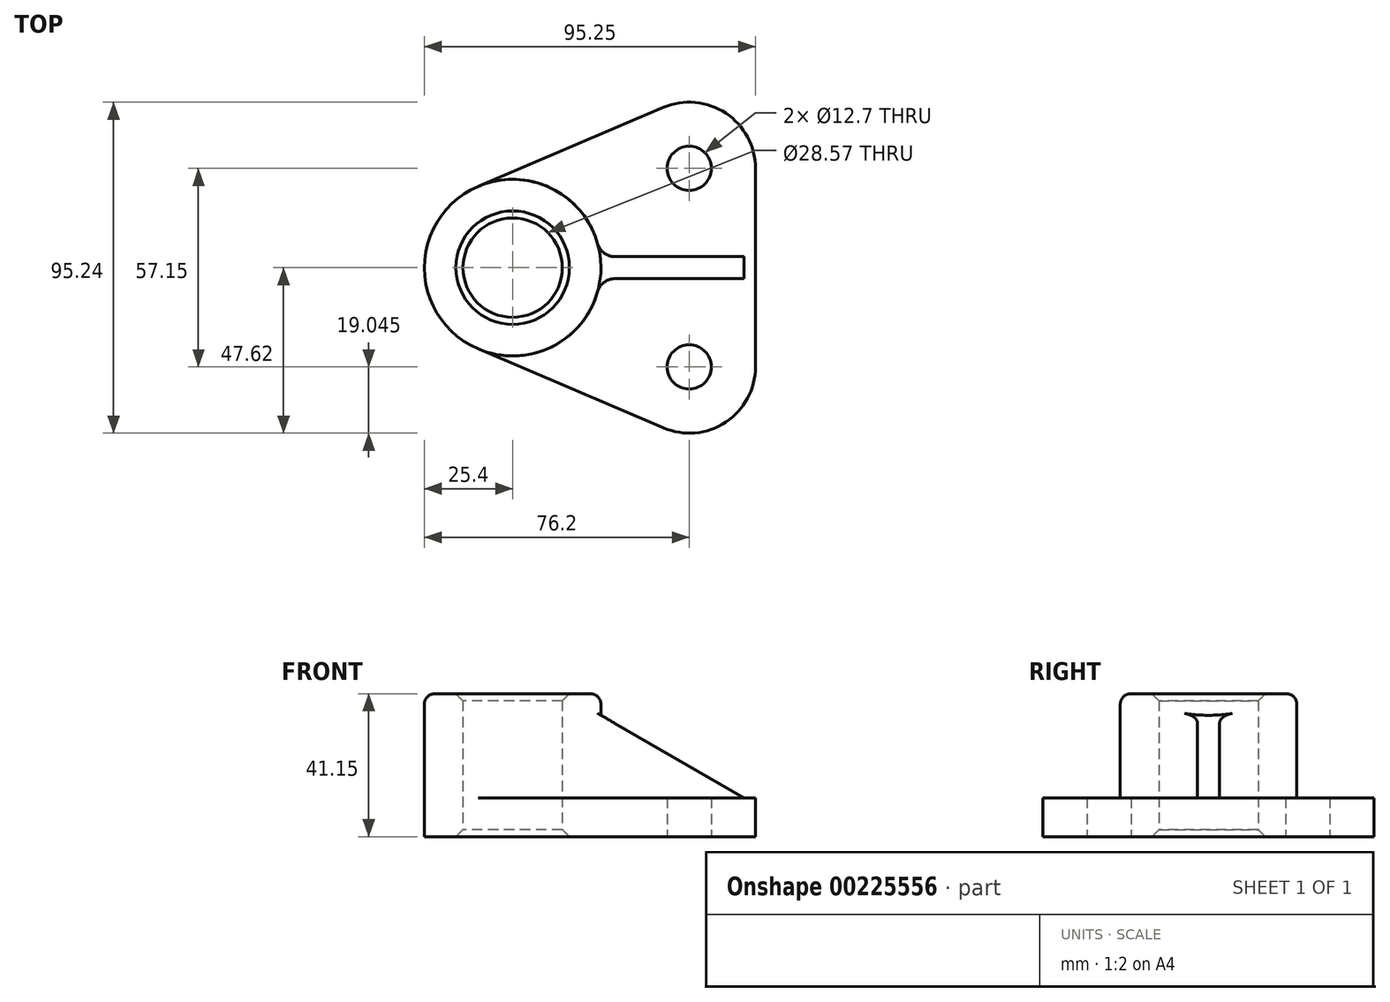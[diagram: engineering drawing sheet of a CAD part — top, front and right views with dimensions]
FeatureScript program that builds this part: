
annotation { "Feature Type Name" : "Feature", "Feature Type Description" : "" }
export const myFeature = defineFeature(function(context is Context, id is Id, definition is map)
    precondition{}
    {
        {
            var Q0;
            Q0=qCreatedBy(makeId("Top.planeOp"),FACE);
            var sketch = newSketch(context, id + "F0", { "sketchPlane" : qUnion([Q0])});
            skCircle(sketch, "E0", {"center": v(0, 0) * mm, "radius": 25.4 * mm});
            skCircle(sketch, "E1", {"center": v(0, 0) * mm, "radius": 14.29 * mm});
            skLineSegment(sketch, "E2", {"start": v(0, 0) * mm, "end": v(50.8, 0) * mm, "construction": true});
            skCircle(sketch, "E3", {"center": v(50.8, 28.58) * mm, "radius": 6.35 * mm});
            skArc(sketch, "E4", {"start": v(69.85, 28.58) * mm, "mid": v(61.3, 44.47) * mm, "end": v(43.33, 46.1) * mm});
            skLineSegment(sketch, "E5", {"start": v(-9.97, 23.36) * mm, "end": v(43.33, 46.1) * mm});
            skLineSegment(sketch, "E6", {"start": v(69.85, 28.58) * mm, "end": v(69.85, 0) * mm});
            skLineSegment(sketch, "E7", {"start": v(50.8, 0) * mm, "end": v(86.08, 0) * mm, "construction": true});
            skLineSegment(sketch, "E8.MirrorCS", {"start": v(-9.97, -23.36) * mm, "end": v(43.33, -46.1) * mm});
            skArc(sketch, "E9.MirrorCS", {"start": v(69.85, -28.58) * mm, "mid": v(61.3, -44.47) * mm, "end": v(43.33, -46.1) * mm});
            skLineSegment(sketch, "E10.MirrorCS", {"start": v(69.85, -28.58) * mm, "end": v(69.85, 0) * mm});
            skCircle(sketch, "E11.MirrorC", {"center": v(50.8, -28.58) * mm, "radius": 6.35 * mm});
            skSolve(sketch);
        }
        {
            var Q0;
            Q0 = qSketchRegion(id + "F0", true);
            extrude(context, id + "F1", {"entities" : qUnion([Q0]), "depth" : 11.18 * mm});
        }
        {
            var Q0;
            Q0=makeQuery(id+"F1.opExtrude","CAP_FACE",FACE,{"disambiguationData":[OSD([sQuery(id+"F0.wireOp",EDGE,"E0"),sQuery(id+"F0.wireOp",EDGE,"E1"),sQuery(id+"F0.wireOp",EDGE,"E3"),sQuery(id+"F0.wireOp",EDGE,"E4"),sQuery(id+"F0.wireOp",EDGE,"E5"),sQuery(id+"F0.wireOp",EDGE,"E6"),sQuery(id+"F0.wireOp",EDGE,"E8.MirrorCS"),sQuery(id+"F0.wireOp",EDGE,"E9.MirrorCS"),sQuery(id+"F0.wireOp",EDGE,"E10.MirrorCS"),sQuery(id+"F0.wireOp",EDGE,"E11.MirrorC")])],"isStart":false});
            var sketch = newSketch(context, id + "F2", { "sketchPlane" : qUnion([Q0])});
            skCircle(sketch, "E12", {"center": v(0, 0) * mm, "radius": 25.4 * mm});
            skCircle(sketch, "E13", {"center": v(0, 0) * mm, "radius": 14.29 * mm});
            skSolve(sketch);
        }
        {
            var Q0;
            Q0 = qSketchRegion(id + "F2", true);
            extrude(context, id + "F3", {"entities" : qUnion([Q0]), "operationType" : NewBodyOperationType.ADD, "depth" : 29.97 * mm});
        }
        {
            var Q0;
            Q0=qCreatedBy(makeId("Front.planeOp"),FACE);
            var sketch = newSketch(context, id + "F4", { "sketchPlane" : qUnion([Q0])});
            skLineSegment(sketch, "E14", {"start": v(18.45, 11.18) * mm, "end": v(66.55, 11.18) * mm});
            skLineSegment(sketch, "E15", {"start": v(66.55, 11.18) * mm, "end": v(18.45, 38.95) * mm});
            skLineSegment(sketch, "E16", {"start": v(18.45, 11.18) * mm, "end": v(18.45, 38.95) * mm});
            skSolve(sketch);
        }
        {
            var Q0;
            Q0 = qSketchRegion(id + "F4", true);
            extrude(context, id + "F5", {"entities" : qUnion([Q0]), "operationType" : NewBodyOperationType.ADD, "endBound" : BoundingType.SYMMETRIC, "depth" : 6.38 * mm});
        }
        {
            var Q0;
            {var subQ0=sQuery(id+"F0.wireOp",EDGE,"E8.MirrorCS");var subQ2=sQuery(id+"F2.wireOp",EDGE,"E12");Q0=makeQuery(id+"F5.boolean.opBoolean","SPLIT",EDGE,{"disambiguationData":[TD([makeQuery(id+"F1.opExtrude","SWEPT_FACE",FACE,{"disambiguationData":[OSD([subQ0])]})])],"derivedFrom":makeQuery(id+"F3.opExtrude","CAP_EDGE",EDGE,{"disambiguationData":[OSD([subQ2])],"isStart":true})});}
            var Q1;
            Q1=makeQuery(id+"F5.opExtrude","CAP_EDGE",EDGE,{"disambiguationData":[OSD([sQuery(id+"F4.wireOp",EDGE,"E14")])],"isStart":false});
            var Q2;
            Q2=makeQuery(id+"F5.boolean.opBoolean","INTERSECT",EDGE,{"derivedFrom":[makeQuery(id+"F3.boolean.opBoolean","MERGE",FACE,{"derivedFrom":[makeQuery(id+"F1.opExtrude","SWEPT_FACE",FACE,{"disambiguationData":[OSD([sQuery(id+"F0.wireOp",EDGE,"E0")])]}),makeQuery(id+"F3.opExtrude","SWEPT_FACE",FACE,{"disambiguationData":[OSD([sQuery(id+"F2.wireOp",EDGE,"E12")])]})]}),makeQuery(id+"F5.opExtrude","CAP_FACE",FACE,{"disambiguationData":[OSD([sQuery(id+"F4.wireOp",EDGE,"E14"),sQuery(id+"F4.wireOp",EDGE,"E15"),sQuery(id+"F4.wireOp",EDGE,"E16")])],"isStart":false})]});
            var Q3;
            {var subQ0=sQuery(id+"F0.wireOp",EDGE,"E5");var subQ2=sQuery(id+"F2.wireOp",EDGE,"E12");Q3=makeQuery(id+"F5.boolean.opBoolean","SPLIT",EDGE,{"disambiguationData":[TD([makeQuery(id+"F1.opExtrude","SWEPT_FACE",FACE,{"disambiguationData":[OSD([subQ0])]})])],"derivedFrom":makeQuery(id+"F3.opExtrude","CAP_EDGE",EDGE,{"disambiguationData":[OSD([subQ2])],"isStart":true})});}
            var Q4;
            Q4=makeQuery(id+"F5.opExtrude","CAP_EDGE",EDGE,{"disambiguationData":[OSD([sQuery(id+"F4.wireOp",EDGE,"E14")])],"isStart":true});
            var Q5;
            Q5=makeQuery(id+"F5.boolean.opBoolean","INTERSECT",EDGE,{"derivedFrom":[makeQuery(id+"F3.boolean.opBoolean","MERGE",FACE,{"derivedFrom":[makeQuery(id+"F1.opExtrude","SWEPT_FACE",FACE,{"disambiguationData":[OSD([sQuery(id+"F0.wireOp",EDGE,"E0")])]}),makeQuery(id+"F3.opExtrude","SWEPT_FACE",FACE,{"disambiguationData":[OSD([sQuery(id+"F2.wireOp",EDGE,"E12")])]})]}),makeQuery(id+"F5.opExtrude","CAP_FACE",FACE,{"disambiguationData":[OSD([sQuery(id+"F4.wireOp",EDGE,"E14"),sQuery(id+"F4.wireOp",EDGE,"E15"),sQuery(id+"F4.wireOp",EDGE,"E16")])],"isStart":true})]});
            fillet(context, id + "F6", {"entities" : qUnion([Q0, Q1, Q2, Q3, Q4, Q5]), "radius" : 5.08 * mm, "tangentPropagation" : true, "allowEdgeOverflow" : false});
        }
        {
            var Q0;
            Q0=makeQuery(id+"F3.opExtrude","CAP_EDGE",EDGE,{"disambiguationData":[OSD([sQuery(id+"F2.wireOp",EDGE,"E12")])],"isStart":false});
            fillet(context, id + "F7", {"entities" : qUnion([Q0]), "radius" : 3.05 * mm, "tangentPropagation" : true, "allowEdgeOverflow" : false});
        }
        {
            var Q0;
            Q0=makeQuery(id+"F3.opExtrude","CAP_EDGE",EDGE,{"disambiguationData":[OSD([sQuery(id+"F2.wireOp",EDGE,"E13")])],"isStart":false});
            var Q1;
            Q1=makeQuery(id+"F1.opExtrude","CAP_EDGE",EDGE,{"disambiguationData":[OSD([sQuery(id+"F0.wireOp",EDGE,"E1")])],"isStart":true});
            chamfer(context, id + "F8", {"entities" : qUnion([Q0, Q1]), "chamferType" : ChamferType.OFFSET_ANGLE, "width" : 2.03 * mm, "oppositeDirection" : false, "angle" : 45 * degree, "tangentPropagation" : true});
        }
    });
